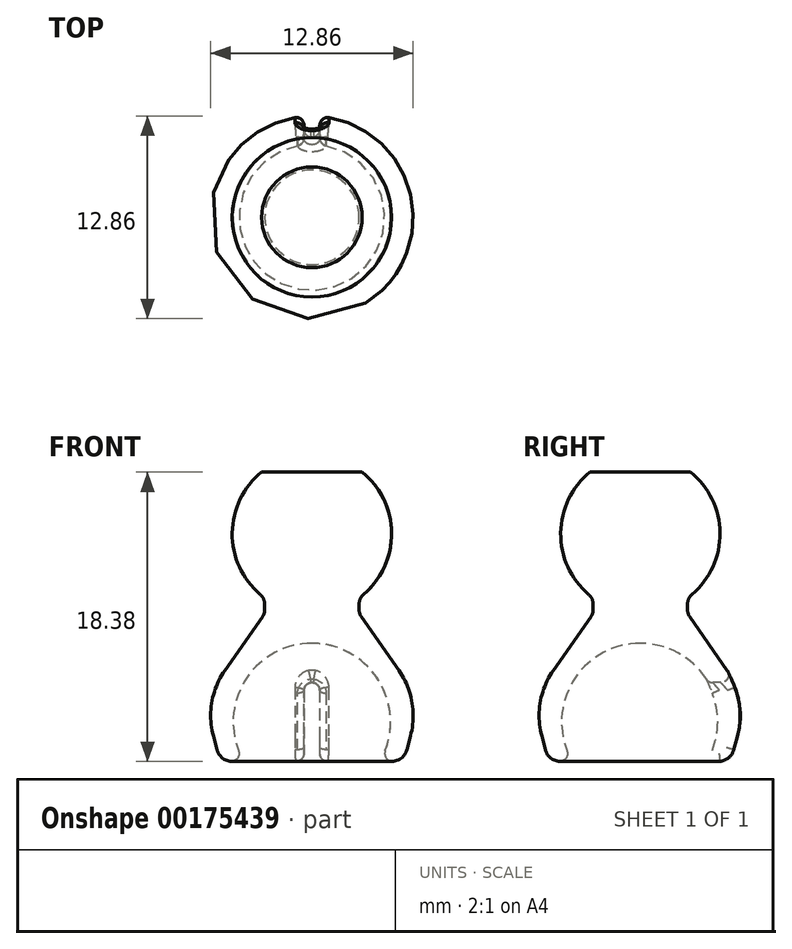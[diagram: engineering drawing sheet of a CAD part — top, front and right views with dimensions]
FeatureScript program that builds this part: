
annotation { "Feature Type Name" : "Feature", "Feature Type Description" : "" }
export const myFeature = defineFeature(function(context is Context, id is Id, definition is map)
    precondition{}
    {
        {
            var Q0;
            Q0=qCreatedBy(makeId("Front.planeOp"),FACE);
            var sketch = newSketch(context, id + "F0", { "sketchPlane" : qUnion([Q0])});
            skLineSegment(sketch, "E0", {"start": v(-3, 9.38) * mm, "end": v(-3, 10.38) * mm});
            skArc(sketch, "E1", {"start": v(0, 19.52) * mm, "mid": v(-4.8, 16.04) * mm, "end": v(-3, 10.38) * mm});
            skLineSegment(sketch, "E2", {"start": v(-5.83, 0) * mm, "end": v(-4.33, 0) * mm});
            skArc(sketch, "E3", {"start": v(0, 7.5) * mm, "mid": v(-4.33, 5) * mm, "end": v(-4.33, 0) * mm});
            skLineSegment(sketch, "E4", {"start": v(-3, 9.38) * mm, "end": v(-6.87, 3.86) * mm});
            skLineSegment(sketch, "E5", {"start": v(-6.87, 3.86) * mm, "end": v(-5.83, 0) * mm});
            skLineSegment(sketch, "E6", {"start": v(0, 19.52) * mm, "end": v(0, 7.5) * mm});
            skSolve(sketch);
        }
        {
            var Q0;
            Q0 = qSketchRegion(id + "F0", true);
            var Q1;
            Q1=sQuery(id+"F0.wireOp",EDGE,"E6");
            revolve(context, id + "F1", {"entities" : qUnion([Q0]), "axis" : qUnion([Q1]), "revolveType" : RevolveType.FULL});
        }
        {
            var Q0;
            Q0=makeQuery(id+"F1.opRevolve","SWEPT_EDGE",EDGE,{"disambiguationData":[OSD([sQuery(id+"F0.wireOp",EDGE,"E4"),sQuery(id+"F0.wireOp",EDGE,"E5")])]});
            fillet(context, id + "F2", {"entities" : qUnion([Q0]), "radius" : 5 * mm, "tangentPropagation" : true, "allowEdgeOverflow" : false});
        }
        {
            var Q0;
            Q0=qCreatedBy(makeId("Front.planeOp"),FACE);
            var sketch = newSketch(context, id + "F3", { "sketchPlane" : qUnion([Q0])});
            skLineSegment(sketch, "E7.bottom", {"start": v(19.78, 26.15) * mm, "end": v(-20.78, 26.15) * mm});
            skLineSegment(sketch, "E7.top", {"start": v(19.78, 18.38) * mm, "end": v(-20.78, 18.38) * mm});
            skLineSegment(sketch, "E7.left", {"start": v(19.78, 26.15) * mm, "end": v(19.78, 18.38) * mm});
            skLineSegment(sketch, "E7.right", {"start": v(-20.78, 26.15) * mm, "end": v(-20.78, 18.38) * mm});
            skSolve(sketch);
        }
        {
            var Q0;
            Q0=makeQuery(id+"F3.imprint","IMPRINT",FACE,{"disambiguationData":[TD([[makeQuery(id+"F3.imprint","IMPRINT",EDGE,{"derivedFrom":sQuery(id+"F3.wireOp",EDGE,"E7.bottom")}),1.0]])]});
            extrude(context, id + "F4", {"entities" : qUnion([Q0]), "operationType" : NewBodyOperationType.REMOVE, "oppositeDirection" : true, "depth" : 25 * mm, "hasSecondDirection" : true, "secondDirectionOppositeDirection" : false, "secondDirectionDepth" : 25 * mm});
        }
        {
            var Q0;
            Q0=makeQuery(id+"F1.opRevolve","SWEPT_EDGE",EDGE,{"disambiguationData":[OSD([sQuery(id+"F0.wireOp",EDGE,"E2"),sQuery(id+"F0.wireOp",EDGE,"E5")])]});
            fillet(context, id + "F5", {"entities" : qUnion([Q0]), "radius" : 1 * mm, "tangentPropagation" : true, "allowEdgeOverflow" : false});
        }
        {
            var Q0;
            Q0=makeQuery(id+"F1.opRevolve","SWEPT_EDGE",EDGE,{"disambiguationData":[OSD([sQuery(id+"F0.wireOp",EDGE,"E0"),sQuery(id+"F0.wireOp",EDGE,"E1")])]});
            var Q1;
            Q1=makeQuery(id+"F1.opRevolve","SWEPT_EDGE",EDGE,{"disambiguationData":[OSD([sQuery(id+"F0.wireOp",EDGE,"E0"),sQuery(id+"F0.wireOp",EDGE,"E4")])]});
            fillet(context, id + "F6", {"entities" : qUnion([Q0, Q1]), "radius" : 0.8 * mm, "tangentPropagation" : true, "allowEdgeOverflow" : false});
        }
        {
            var Q0;
            Q0=makeQuery(id+"F1.opRevolve","SWEPT_EDGE",EDGE,{"disambiguationData":[OSD([sQuery(id+"F0.wireOp",EDGE,"E2"),sQuery(id+"F0.wireOp",EDGE,"E3")])]});
            fillet(context, id + "F7", {"entities" : qUnion([Q0]), "radius" : 0.5 * mm, "tangentPropagation" : true, "allowEdgeOverflow" : false});
        }
        {
            var Q0;
            Q0=qCreatedBy(makeId("Front.planeOp"),FACE);
            var sketch = newSketch(context, id + "F8", { "sketchPlane" : qUnion([Q0])});
            skLineSegment(sketch, "E8.bottom", {"start": v(-0.5, 5) * mm, "end": v(0.5, 5) * mm});
            skLineSegment(sketch, "E8.top", {"start": v(-0.5, -3.42) * mm, "end": v(0.5, -3.42) * mm});
            skLineSegment(sketch, "E8.left", {"start": v(-0.5, 5) * mm, "end": v(-0.5, -3.42) * mm});
            skLineSegment(sketch, "E8.right", {"start": v(0.5, 5) * mm, "end": v(0.5, -3.42) * mm});
            skPoint(sketch, "E8.middle", {"position": v(0, 0.8) * mm});
            skSolve(sketch);
        }
        {
            var Q0;
            Q0=makeQuery(id+"F8.imprint","IMPRINT",FACE,{"disambiguationData":[TD([[makeQuery(id+"F8.imprint","IMPRINT",EDGE,{"derivedFrom":sQuery(id+"F8.wireOp",EDGE,"E8.bottom")}),-1.0]])]});
            extrude(context, id + "F9", {"entities" : qUnion([Q0]), "operationType" : NewBodyOperationType.REMOVE, "oppositeDirection" : true, "depth" : 25 * mm});
        }
        {
            var Q0;
            Q0=makeQuery(id+"F9.boolean.opBoolean","COPY",EDGE,{"derivedFrom":makeQuery(id+"F9.opExtrude","SWEPT_EDGE",EDGE,{"disambiguationData":[OSD([sQuery(id+"F8.wireOp",EDGE,"E8.bottom"),sQuery(id+"F8.wireOp",EDGE,"E8.left")])]})});
            var Q1;
            Q1=makeQuery(id+"F9.boolean.opBoolean","COPY",EDGE,{"derivedFrom":makeQuery(id+"F9.opExtrude","SWEPT_EDGE",EDGE,{"disambiguationData":[OSD([sQuery(id+"F8.wireOp",EDGE,"E8.bottom"),sQuery(id+"F8.wireOp",EDGE,"E8.right")])]})});
            fillet(context, id + "F10", {"entities" : qUnion([Q0, Q1]), "radius" : 0.5 * mm, "tangentPropagation" : true, "allowEdgeOverflow" : false});
        }
        {
            var Q0;
            Q0=makeQuery(id+"F9.boolean.opBoolean","INTERSECT",EDGE,{"derivedFrom":[makeQuery(id+"F2.opFillet","BLEND_FACE",FACE,{"disambiguationData":[OSD([sQuery(id+"F0.wireOp",EDGE,"E4"),sQuery(id+"F0.wireOp",EDGE,"E5")])]}),makeQuery(id+"F9.opExtrude","SWEPT_FACE",FACE,{"disambiguationData":[OSD([sQuery(id+"F8.wireOp",EDGE,"E8.left")])]})]});
            fillet(context, id + "F11", {"entities" : qUnion([Q0]), "radius" : 0.5 * mm, "tangentPropagation" : true, "allowEdgeOverflow" : false});
        }
    });
